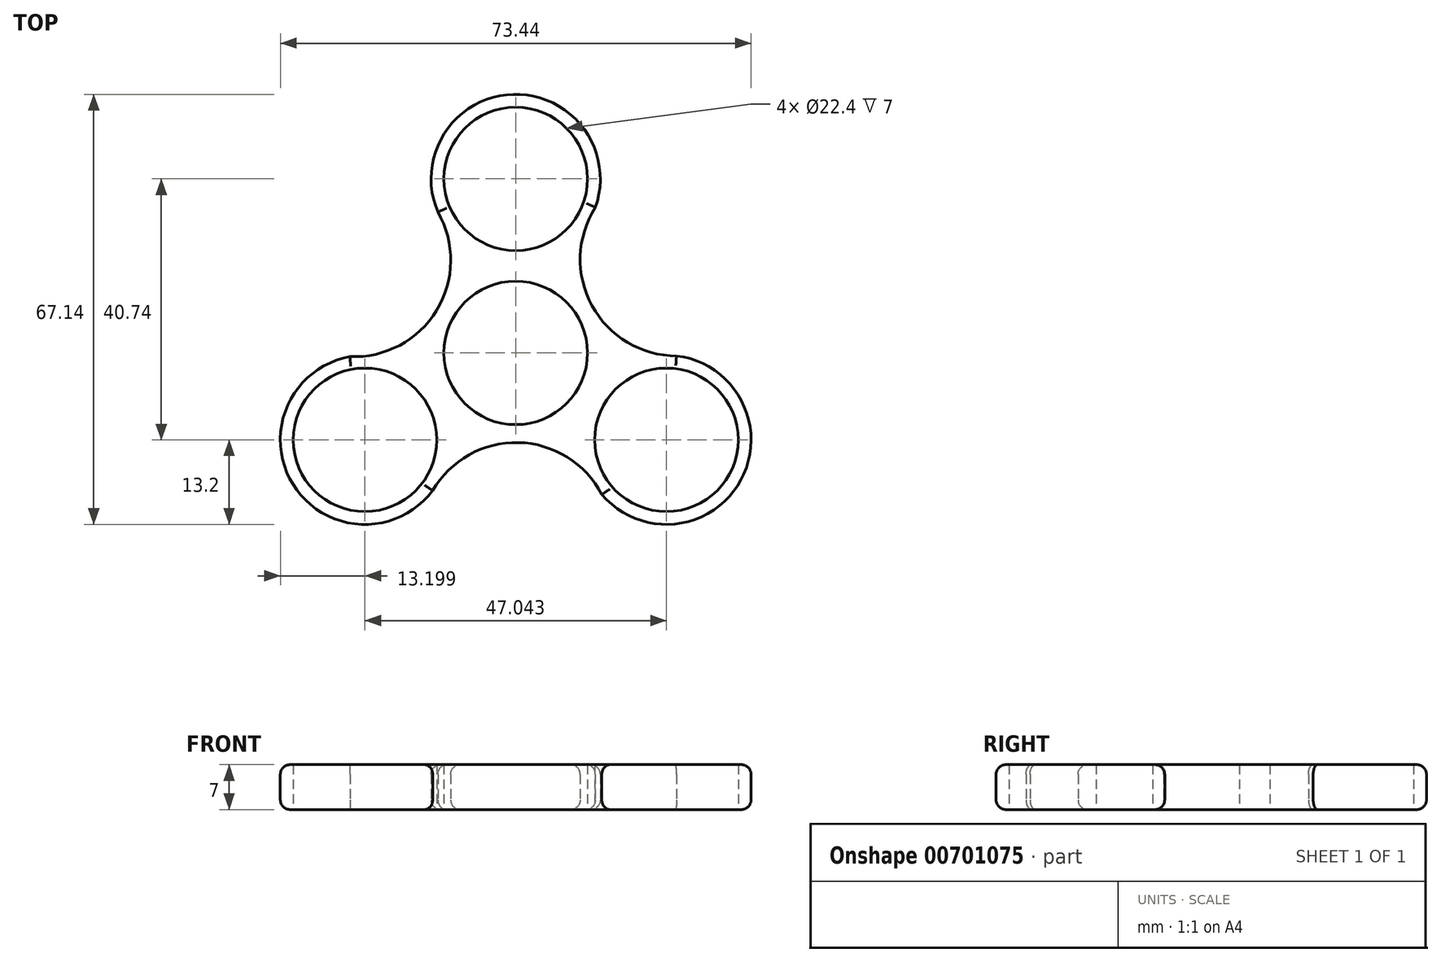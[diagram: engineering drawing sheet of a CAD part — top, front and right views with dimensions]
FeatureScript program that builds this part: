
annotation { "Feature Type Name" : "Feature", "Feature Type Description" : "" }
export const myFeature = defineFeature(function(context is Context, id is Id, definition is map)
    precondition{}
    {
        {
            var Q0;
            Q0=qCreatedBy(makeId("Top.planeOp"),FACE);
            var sketch = newSketch(context, id + "F0", { "sketchPlane" : qUnion([Q0])});
            skCircle(sketch, "E0", {"center": v(0, 0) * mm, "radius": 11.2 * mm});
            skCircle(sketch, "E1", {"center": v(0, 27.16) * mm, "radius": 11.2 * mm});
            skArc(sketch, "E2", {"start": v(11.03, 19.91) * mm, "mid": v(0.35, 40.36) * mm, "end": v(-11.4, 20.51) * mm});
            skCircle(sketch, "E3.1.0", {"center": v(-23.52, -13.58) * mm, "radius": 11.2 * mm});
            skArc(sketch, "E3.1.1", {"start": v(-22.76, -0.4) * mm, "mid": v(-35.13, -19.87) * mm, "end": v(-12.06, -20.13) * mm});
            skCircle(sketch, "E3.2.0", {"center": v(23.52, -13.58) * mm, "radius": 11.2 * mm});
            skArc(sketch, "E3.2.1", {"start": v(11.73, -19.5) * mm, "mid": v(34.77, -20.48) * mm, "end": v(23.47, -0.38) * mm});
            skArc(sketch, "E4", {"start": v(12.42, 22.69) * mm, "mid": v(11.91, 7.37) * mm, "end": v(25.08, -0.47) * mm});
            skArc(sketch, "E5.1.0", {"start": v(-25.86, -0.59) * mm, "mid": v(-12.34, 6.63) * mm, "end": v(-12.13, 21.96) * mm});
            skArc(sketch, "E5.2.0", {"start": v(13.44, -22.1) * mm, "mid": v(0.43, -14) * mm, "end": v(-12.95, -21.49) * mm});
            skSolve(sketch);
        }
        {
            var Q0;
            Q0=makeQuery(id+"F0.imprint","IMPRINT",FACE,{"disambiguationData":[TD([[makeQuery(id+"F0.imprint","IMPRINT",EDGE,{"derivedFrom":sQuery(id+"F0.wireOp",EDGE,"E0")}),-1.0]])]});
            extrude(context, id + "F1", {"entities" : qUnion([Q0]), "depth" : 7 * mm, "offsetDistance" : 25 * mm});
        }
        {
            var Q0;
            Q0=makeQuery(id+"F1.opExtrude","CAP_EDGE",EDGE,{"disambiguationData":[OSD([sQuery(id+"F0.wireOp",EDGE,"E3.1.1")])],"isStart":false});
            var Q1;
            Q1=makeQuery(id+"F1.opExtrude","CAP_EDGE",EDGE,{"disambiguationData":[OSD([sQuery(id+"F0.wireOp",EDGE,"E5.1.0")])],"isStart":false});
            var Q2;
            Q2=makeQuery(id+"F1.opExtrude","CAP_EDGE",EDGE,{"disambiguationData":[OSD([sQuery(id+"F0.wireOp",EDGE,"E2")])],"isStart":false});
            var Q3;
            Q3=makeQuery(id+"F1.opExtrude","CAP_EDGE",EDGE,{"disambiguationData":[OSD([sQuery(id+"F0.wireOp",EDGE,"E4")])],"isStart":false});
            var Q4;
            Q4=makeQuery(id+"F1.opExtrude","CAP_EDGE",EDGE,{"disambiguationData":[OSD([sQuery(id+"F0.wireOp",EDGE,"E3.2.1")])],"isStart":false});
            var Q5;
            Q5=makeQuery(id+"F1.opExtrude","CAP_EDGE",EDGE,{"disambiguationData":[OSD([sQuery(id+"F0.wireOp",EDGE,"E5.2.0")])],"isStart":false});
            fillet(context, id + "F2", {"entities" : qUnion([Q0, Q1, Q2, Q3, Q4, Q5]), "radius" : 1.5 * mm, "tangentPropagation" : true, "allowEdgeOverflow" : false});
        }
        {
            var Q0;
            Q0=makeQuery(id+"F1.opExtrude","CAP_EDGE",EDGE,{"disambiguationData":[OSD([sQuery(id+"F0.wireOp",EDGE,"E2")])],"isStart":true});
            var Q1;
            Q1=makeQuery(id+"F1.opExtrude","CAP_EDGE",EDGE,{"disambiguationData":[OSD([sQuery(id+"F0.wireOp",EDGE,"E5.1.0")])],"isStart":true});
            var Q2;
            Q2=makeQuery(id+"F1.opExtrude","CAP_EDGE",EDGE,{"disambiguationData":[OSD([sQuery(id+"F0.wireOp",EDGE,"E3.1.1")])],"isStart":true});
            var Q3;
            Q3=makeQuery(id+"F1.opExtrude","CAP_EDGE",EDGE,{"disambiguationData":[OSD([sQuery(id+"F0.wireOp",EDGE,"E5.2.0")])],"isStart":true});
            var Q4;
            Q4=makeQuery(id+"F1.opExtrude","CAP_EDGE",EDGE,{"disambiguationData":[OSD([sQuery(id+"F0.wireOp",EDGE,"E3.2.1")])],"isStart":true});
            var Q5;
            Q5=makeQuery(id+"F1.opExtrude","CAP_EDGE",EDGE,{"disambiguationData":[OSD([sQuery(id+"F0.wireOp",EDGE,"E4")])],"isStart":true});
            fillet(context, id + "F3", {"entities" : qUnion([Q0, Q1, Q2, Q3, Q4, Q5]), "radius" : 1.5 * mm, "tangentPropagation" : true, "allowEdgeOverflow" : false});
        }
    });
